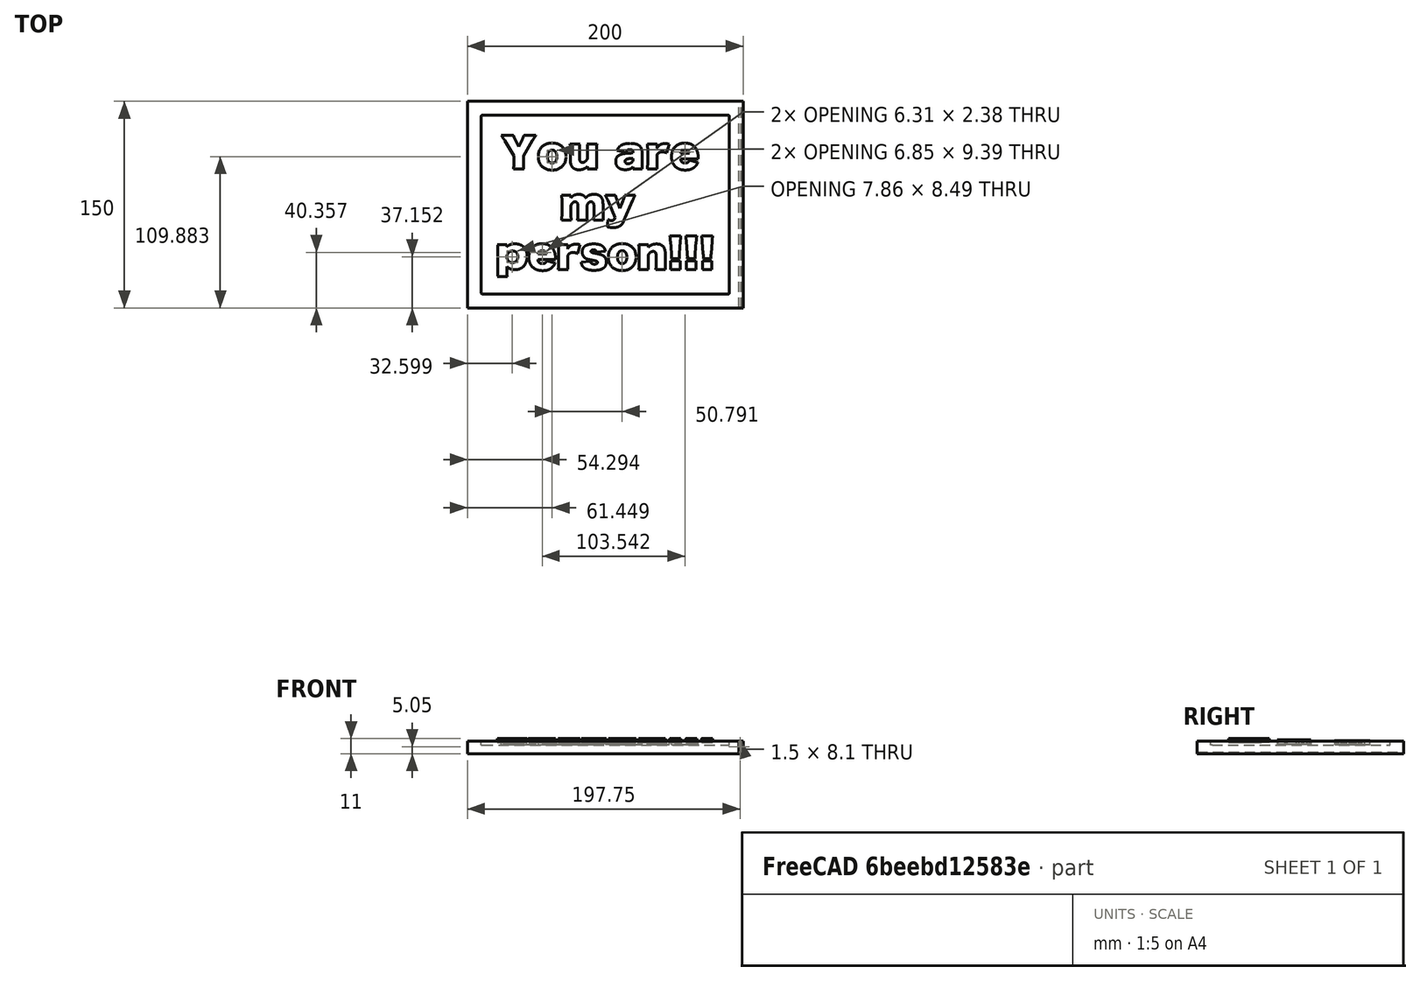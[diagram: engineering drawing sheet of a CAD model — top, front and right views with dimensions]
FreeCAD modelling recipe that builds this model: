
FCSTD DOCUMENT  (FreeCAD 0.21R33694 (Git))
Label: my_person
License: Creative Commons Attribution 4.0
LicenseURL: https://creativecommons.org/licenses/by/4.0/
objects: Part::Part2DObjectPython×3, Part::Extrusion×3, PartDesign::SubtractiveBox×2, PartDesign::AdditiveBox×1, PartDesign::Fillet×1, PartDesign::Body×1
note: 15 computed .brp shape members not serialized (recipe doc carries the construction recipe); baked Part::Feature solids carry a one-line shape summary decoded from their .brp

FEATURE [PartDesign::AdditiveBox] Box004
  AttacherType = Attacher::AttachEngine3D
  Height = 9.2
  Length = 200
  MapMode = 5
  Support = -> [XY_Plane001]
  Width = 150
FEATURE [PartDesign::SubtractiveBox] Box005
  AttacherType = Attacher::AttachEngine3D
  AttachmentOffset = pos=(10,10,-3.06667) rot=(0,0,1;0rad)
  BaseFeature = -> Box004
  Height = 3.06667
  Length = 180
  MapMode = 5
  Placement = pos=(10,10,6.13333) rot=(0,0,1;0rad)
  Support = -> [Box004]
  Width = 130
  expr: .AttachmentOffset.Base.x = (<<Box004>>.Length - Length) / 2
  expr: .AttachmentOffset.Base.y = (<<Box004>>.Width - Width) / 2
  expr: .AttachmentOffset.Base.z = -Height
  expr: Height = <<Box004>>.Height / 3
  expr: Length = <<Box004>>.Length - 20 mm
  expr: Width = <<Box004>>.Width - 20 mm
FEATURE [Part::Part2DObjectPython] ShapeString003  # Draft 2D object (typed FeaturePython)
  FontFile = /System/Library/Fonts/ヒラギノ角ゴシック W9.ttc
  Fuse = false
  Justification = 1
  JustificationReference = 0
  KeepLeftMargin = false
  MakeFace = true
  ObliqueAngle = 0
  Placement = pos=(24.5,102,6.5) rot=(0,0,1;0rad)
  ScaleToSize = true
  Size = 14
  String = You are
  Tracking = 1
  expr: .Placement.Base.y = Box004.Width - (Box004.Width - Box005.Width) - Size * 2
FEATURE [PartDesign::Fillet] Fillet
  Base = -> Box005 [Edge18,Edge22,Edge17,Edge21]
  BaseFeature = -> Box005
  Placement = pos=(10,10,6.13333) rot=(0,0,1;0rad)
  Radius = 1
  SupportTransform = false
  UseAllEdges = false
FEATURE [PartDesign::SubtractiveBox] Box007
  AttacherType = Attacher::AttachEngine3D
  AttachmentOffset = pos=(197,0,1) rot=(0,0,1;0rad)
  BaseFeature = -> Fillet
  Height = 8.1
  Length = 1.5
  MapMode = 5
  Placement = pos=(197,0,1) rot=(0,0,1;0rad)
  Support = -> [XY_Plane001]
  Width = 150
  expr: .AttachmentOffset.Base.x = Box004.Length - 3 mm
  expr: Width = Box004.Width
FEATURE [PartDesign::Body] Body001
  Group = -> [Box004,Box005,Fillet,Box007]
  Origin = -> Origin001
  Tip = -> Box007
FEATURE [Part::Part2DObjectPython] ShapeString  # Draft 2D object (typed FeaturePython)
  FontFile = /System/Library/Fonts/ヒラギノ角ゴシック W9.ttc
  MakeFace = true
  Placement = pos=(20.5,29,8) rot=(0,0,1;0rad)
  Size = 14
  String = person!!!
  Tracking = 0
FEATURE [Part::Part2DObjectPython] ShapeString004  # Draft 2D object (typed FeaturePython)
  FontFile = /System/Library/Fonts/ヒラギノ角ゴシック W9.ttc
  MakeFace = true
  Placement = pos=(66.97,65,7) rot=(0,0,-1;0.000175rad)
  Size = 14
  String = my
  Tracking = 0
  expr: .Placement.Base.y = Box005.Width / 2
FEATURE [Part::Extrusion] Extrude
  Base = -> ShapeString003
  Dir = (0,0,1)
  DirMode = 2
  FaceMakerClass = Part::FaceMakerBullseye
  LengthFwd = 3
  LengthRev = 0
  Solid = false
  Symmetric = false
FEATURE [Part::Extrusion] Extrude001
  Base = -> ShapeString
  Dir = (0,0,1)
  DirMode = 2
  FaceMakerClass = Part::FaceMakerBullseye
  LengthFwd = 3
  LengthRev = 0
  Solid = false
  Symmetric = false
FEATURE [Part::Extrusion] Extrude002
  Base = -> ShapeString004
  Dir = (0,0,1)
  DirMode = 2
  FaceMakerClass = Part::FaceMakerBullseye
  LengthFwd = 3
  LengthRev = 0
  Solid = false
  Symmetric = false
